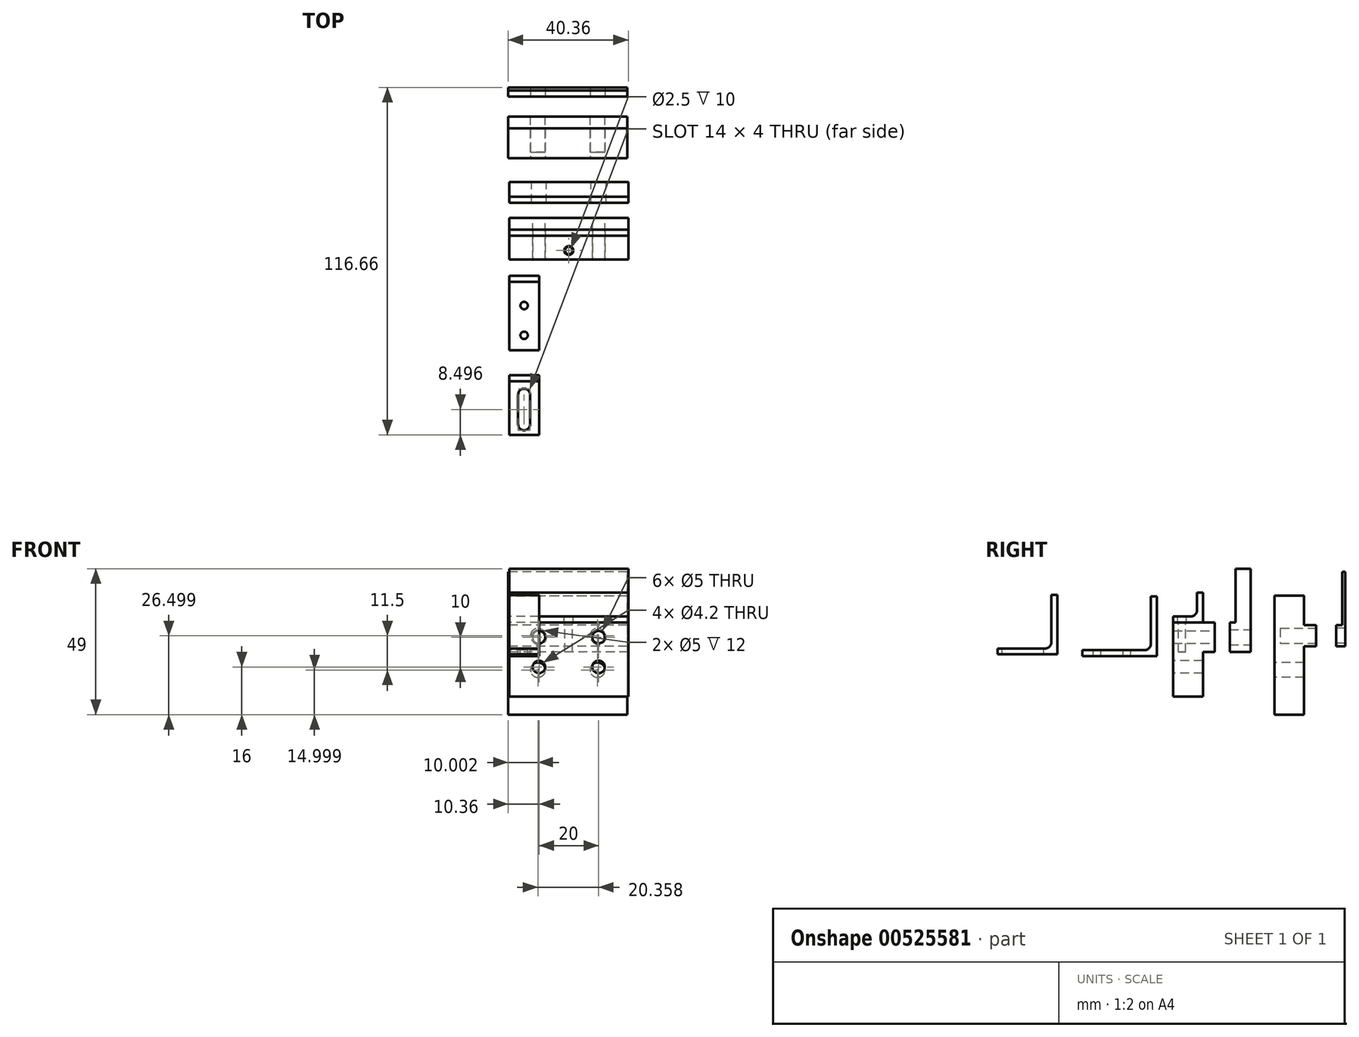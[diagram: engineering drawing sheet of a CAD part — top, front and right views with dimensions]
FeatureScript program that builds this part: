
annotation { "Feature Type Name" : "Feature", "Feature Type Description" : "" }
export const myFeature = defineFeature(function(context is Context, id is Id, definition is map)
    precondition{}
    {
        {
            var Q0;
            Q0=qCreatedBy(makeId("Right.planeOp"),FACE);
            cPlane(context, id + "F0", {"entities" : qUnion([Q0]), "cplaneType" : CPlaneType.OFFSET, "offset" : 40 * mm, "oppositeDirection" : true, "width" : 150 * mm, "height" : 150 * mm});
        }
        {
            var Q0;
            Q0=qCreatedBy(makeId("Front.planeOp"),FACE);
            var sketch = newSketch(context, id + "F1", { "sketchPlane" : qUnion([Q0])});
            skLineSegment(sketch, "E0.bottom", {"start": v(-40.36, 24) * mm, "end": v(-0.36, 24) * mm});
            skLineSegment(sketch, "E0.top", {"start": v(-40.36, -16) * mm, "end": v(-0.36, -16) * mm});
            skLineSegment(sketch, "E0.left", {"start": v(-40.36, 24) * mm, "end": v(-40.36, -16) * mm});
            skLineSegment(sketch, "E0.right", {"start": v(-0.36, 24) * mm, "end": v(-0.36, -16) * mm});
            skCircle(sketch, "E1", {"center": v(-10.36, -1) * mm, "radius": 2.5 * mm});
            skCircle(sketch, "E2", {"center": v(-30.36, -1) * mm, "radius": 2.5 * mm});
            skCircle(sketch, "E3", {"center": v(-30.36, -1) * mm, "radius": 6 * mm, "construction": true});
            skCircle(sketch, "E4", {"center": v(-10.36, -1) * mm, "radius": 6 * mm, "construction": true});
            skSolve(sketch);
        }
        {
            var Q0;
            Q0=qSketchRegion(id+"F1",true);
            extrude(context, id + "F2", {"entities" : qUnion([Q0]), "oppositeDirection" : true, "depth" : 10 * mm});
        }
        {
            var Q0;
            Q0=makeQuery(id+"F2.opExtrude","CAP_FACE",FACE,{"disambiguationData":[OSD([sQuery(id+"F1.wireOp",EDGE,"E0.bottom"),sQuery(id+"F1.wireOp",EDGE,"E0.top"),sQuery(id+"F1.wireOp",EDGE,"E0.left"),sQuery(id+"F1.wireOp",EDGE,"E0.right"),sQuery(id+"F1.wireOp",EDGE,"E1"),sQuery(id+"F1.wireOp",EDGE,"E2")])],"isStart":false});
            var sketch = newSketch(context, id + "F3", { "sketchPlane" : qUnion([Q0])});
            skLineSegment(sketch, "E5.bottom", {"start": v(0.36, 14) * mm, "end": v(40.36, 14) * mm});
            skLineSegment(sketch, "E5.top", {"start": v(0.36, 7) * mm, "end": v(40.36, 7) * mm});
            skLineSegment(sketch, "E5.left", {"start": v(0.36, 14) * mm, "end": v(0.36, 7) * mm});
            skLineSegment(sketch, "E5.right", {"start": v(40.36, 14) * mm, "end": v(40.36, 7) * mm});
            skSolve(sketch);
        }
        {
            var Q0;
            Q0=qSketchRegion(id+"F3",true);
            extrude(context, id + "F4", {"entities" : qUnion([Q0]), "operationType" : NewBodyOperationType.ADD, "depth" : 4 * mm});
        }
        {
            var Q0;
            Q0=makeQuery(id+"F4.opExtrude","CAP_FACE",FACE,{"disambiguationData":[OSD([sQuery(id+"F3.wireOp",EDGE,"E5.bottom"),sQuery(id+"F3.wireOp",EDGE,"E5.top"),sQuery(id+"F3.wireOp",EDGE,"E5.left"),sQuery(id+"F3.wireOp",EDGE,"E5.right")])],"isStart":false});
            var sketch = newSketch(context, id + "F5", { "sketchPlane" : qUnion([Q0])});
            skCircle(sketch, "E6", {"center": v(10.36, 10.5) * mm, "radius": 2.5 * mm});
            skCircle(sketch, "E7", {"center": v(30.36, 10.5) * mm, "radius": 2.5 * mm});
            skSolve(sketch);
        }
        {
            var Q0;
            Q0=qSketchRegion(id+"F5",true);
            extrude(context, id + "F6", {"entities" : qUnion([Q0]), "operationType" : NewBodyOperationType.REMOVE, "oppositeDirection" : true, "depth" : 12 * mm});
        }
        {
            var Q0;
            Q0=makeQuery(id+"F4.boolean.opBoolean","MERGE",FACE,{"derivedFrom":[makeQuery(id+"F2.opExtrude","SWEPT_FACE",FACE,{"disambiguationData":[OSD([sQuery(id+"F1.wireOp",EDGE,"E0.left")])]}),makeQuery(id+"F4.opExtrude","SWEPT_FACE",FACE,{"disambiguationData":[OSD([sQuery(id+"F3.wireOp",EDGE,"E5.right")])]})]});
            var sketch = newSketch(context, id + "F7", { "sketchPlane" : qUnion([Q0])});
            skLineSegment(sketch, "E8", {"start": v(-23.76, 32) * mm, "end": v(-23.76, 7) * mm});
            skLineSegment(sketch, "E9", {"start": v(-20.76, 7) * mm, "end": v(-23.76, 7) * mm});
            skLineSegment(sketch, "E10", {"start": v(-20.76, 7) * mm, "end": v(-20.76, 14) * mm});
            skLineSegment(sketch, "E11", {"start": v(-22.76, 14) * mm, "end": v(-20.76, 14) * mm});
            skLineSegment(sketch, "E12", {"start": v(-22.76, 14) * mm, "end": v(-22.76, 32) * mm});
            skLineSegment(sketch, "E13", {"start": v(-23.76, 32) * mm, "end": v(-22.76, 32) * mm});
            skSolve(sketch);
        }
        {
            var Q0;
            Q0=makeQuery(id+"F7.imprint","IMPRINT",FACE,{"disambiguationData":[TD([[makeQuery(id+"F7.imprint","IMPRINT",EDGE,{"derivedFrom":sQuery(id+"F7.wireOp",EDGE,"E8")}),1.0]])]});
            extrude(context, id + "F8", {"entities" : qUnion([Q0]), "oppositeDirection" : true, "depth" : 40 * mm});
        }
        {
            var Q0;
            Q0=makeQuery(id+"F8.opExtrude","SWEPT_FACE",FACE,{"disambiguationData":[OSD([sQuery(id+"F7.wireOp",EDGE,"E10")])]});
            var sketch = newSketch(context, id + "F9", { "sketchPlane" : qUnion([Q0])});
            skCircle(sketch, "E14", {"center": v(-30.36, 10.5) * mm, "radius": 2.5 * mm});
            skCircle(sketch, "E15", {"center": v(-10.36, 10.5) * mm, "radius": 2.5 * mm});
            skSolve(sketch);
        }
        {
            var Q0;
            Q0=makeQuery(id+"F9.imprint","IMPRINT",FACE,{"disambiguationData":[TD([[makeQuery(id+"F9.imprint","IMPRINT",EDGE,{"derivedFrom":sQuery(id+"F9.wireOp",EDGE,"E14")}),1.0]])]});
            var Q1;
            Q1=makeQuery(id+"F9.imprint","IMPRINT",FACE,{"disambiguationData":[TD([[makeQuery(id+"F9.imprint","IMPRINT",EDGE,{"derivedFrom":sQuery(id+"F9.wireOp",EDGE,"E15")}),1.0]])]});
            extrude(context, id + "F10", {"entities" : qUnion([Q0, Q1]), "operationType" : NewBodyOperationType.REMOVE, "oppositeDirection" : true, "depth" : 3 * mm});
        }
        {
            var Q0;
            Q0=qCreatedBy(id+"F0.planeOp",FACE);
            var sketch = newSketch(context, id + "F11", { "sketchPlane" : qUnion([Q0])});
            skLineSegment(sketch, "E16", {"start": v(-20, 15) * mm, "end": v(-34, 15) * mm});
            skLineSegment(sketch, "E17", {"start": v(-34, 15) * mm, "end": v(-34, -10) * mm});
            skLineSegment(sketch, "E18", {"start": v(-34, -10) * mm, "end": v(-24, -10) * mm});
            skLineSegment(sketch, "E19", {"start": v(-24, -10) * mm, "end": v(-24, 5) * mm});
            skLineSegment(sketch, "E20", {"start": v(-24, 5) * mm, "end": v(-20, 5) * mm});
            skLineSegment(sketch, "E21", {"start": v(-20, 5) * mm, "end": v(-20, 15) * mm});
            skSolve(sketch);
        }
        {
            var Q0;
            Q0=qSketchRegion(id+"F11",true);
            extrude(context, id + "F12", {"entities" : qUnion([Q0]), "depth" : 40 * mm});
        }
        {
            var Q0;
            Q0=qCreatedBy(id+"F0.planeOp",FACE);
            var sketch = newSketch(context, id + "F13", { "sketchPlane" : qUnion([Q0])});
            skLineSegment(sketch, "E22", {"start": v(-8, 33) * mm, "end": v(-8, 5) * mm});
            skLineSegment(sketch, "E23", {"start": v(-8, 5) * mm, "end": v(-15, 5) * mm});
            skLineSegment(sketch, "E24", {"start": v(-15, 5) * mm, "end": v(-15, 15) * mm});
            skLineSegment(sketch, "E25", {"start": v(-15, 15) * mm, "end": v(-13, 15) * mm});
            skLineSegment(sketch, "E26", {"start": v(-13, 15) * mm, "end": v(-13, 33) * mm});
            skLineSegment(sketch, "E27", {"start": v(-13, 33) * mm, "end": v(-8, 33) * mm});
            skSolve(sketch);
        }
        {
            var Q0;
            Q0=makeQuery(id+"F13.imprint","IMPRINT",FACE,{"disambiguationData":[TD([[makeQuery(id+"F13.imprint","IMPRINT",EDGE,{"derivedFrom":sQuery(id+"F13.wireOp",EDGE,"E22")}),-1.0]])]});
            extrude(context, id + "F14", {"entities" : qUnion([Q0]), "depth" : 40 * mm});
        }
        {
            var Q0;
            Q0=makeQuery(id+"F12.opExtrude","SWEPT_FACE",FACE,{"disambiguationData":[OSD([sQuery(id+"F11.wireOp",EDGE,"E17")])]});
            var sketch = newSketch(context, id + "F15", { "sketchPlane" : qUnion([Q0])});
            skCircle(sketch, "E28", {"center": v(-30, 0) * mm, "radius": 2.1 * mm});
            skCircle(sketch, "E29", {"center": v(-10, 0) * mm, "radius": 2.1 * mm});
            skSolve(sketch);
        }
        {
            var Q0;
            Q0=makeQuery(id+"F14.opExtrude","SWEPT_FACE",FACE,{"disambiguationData":[OSD([sQuery(id+"F13.wireOp",EDGE,"E22")])]});
            var sketch = newSketch(context, id + "F16", { "sketchPlane" : qUnion([Q0])});
            skCircle(sketch, "E30", {"center": v(10, 10) * mm, "radius": 2.5 * mm});
            skCircle(sketch, "E31", {"center": v(30, 10) * mm, "radius": 2.5 * mm});
            skSolve(sketch);
        }
        {
            var Q0;
            Q0=qCreatedBy(id+"F0.planeOp",FACE);
            var sketch = newSketch(context, id + "F17", { "sketchPlane" : qUnion([Q0])});
            skLineSegment(sketch, "E32", {"start": v(-24, 25) * mm, "end": v(-24, 15) * mm});
            skLineSegment(sketch, "E33", {"start": v(-24, 15) * mm, "end": v(-34, 15) * mm});
            skLineSegment(sketch, "E34", {"start": v(-34, 15) * mm, "end": v(-34, 17) * mm});
            skLineSegment(sketch, "E35", {"start": v(-34, 17) * mm, "end": v(-28, 17) * mm});
            skLineSegment(sketch, "E36", {"start": v(-26, 19) * mm, "end": v(-26, 25) * mm});
            skLineSegment(sketch, "E37", {"start": v(-26, 25) * mm, "end": v(-24, 25) * mm});
            skPoint(sketch, "E38.visualSharp", {"position": v(-26, 17) * mm});
            skArc(sketch, "E38.filletArc", {"start": v(-28, 17) * mm, "mid": v(-26.59, 17.59) * mm, "end": v(-26, 19) * mm});
            skSolve(sketch);
        }
        {
            var Q0;
            Q0=makeQuery(id+"F17.imprint","IMPRINT",FACE,{"disambiguationData":[TD([[makeQuery(id+"F17.imprint","IMPRINT",EDGE,{"derivedFrom":sQuery(id+"F17.wireOp",EDGE,"E32")}),-1.0]])]});
            extrude(context, id + "F18", {"entities" : qUnion([Q0]), "depth" : 40 * mm});
        }
        {
            var Q0;
            Q0=makeQuery(id+"F18.opExtrude","SWEPT_FACE",FACE,{"disambiguationData":[OSD([sQuery(id+"F17.wireOp",EDGE,"E35")])]});
            var sketch = newSketch(context, id + "F19", { "sketchPlane" : qUnion([Q0])});
            skCircle(sketch, "E39", {"center": v(-20, -31) * mm, "radius": 1.25 * mm});
            skSolve(sketch);
        }
        {
            var Q0;
            Q0=makeQuery(id+"F15.imprint","IMPRINT",FACE,{"disambiguationData":[TD([[makeQuery(id+"F15.imprint","IMPRINT",EDGE,{"derivedFrom":sQuery(id+"F15.wireOp",EDGE,"E28")}),1.0]])]});
            var Q1;
            Q1=makeQuery(id+"F15.imprint","IMPRINT",FACE,{"disambiguationData":[TD([[makeQuery(id+"F15.imprint","IMPRINT",EDGE,{"derivedFrom":sQuery(id+"F15.wireOp",EDGE,"E29")}),1.0]])]});
            extrude(context, id + "F20", {"entities" : qUnion([Q0, Q1]), "operationType" : NewBodyOperationType.REMOVE, "oppositeDirection" : true, "depth" : 10 * mm});
        }
        {
            var Q0;
            Q0=makeQuery(id+"F16.imprint","IMPRINT",FACE,{"disambiguationData":[TD([[makeQuery(id+"F16.imprint","IMPRINT",EDGE,{"derivedFrom":sQuery(id+"F16.wireOp",EDGE,"E30")}),1.0]])]});
            var Q1;
            Q1=makeQuery(id+"F16.imprint","IMPRINT",FACE,{"disambiguationData":[TD([[makeQuery(id+"F16.imprint","IMPRINT",EDGE,{"derivedFrom":sQuery(id+"F16.wireOp",EDGE,"E31")}),1.0]])]});
            extrude(context, id + "F21", {"entities" : qUnion([Q0, Q1]), "operationType" : NewBodyOperationType.REMOVE, "oppositeDirection" : true, "depth" : 7 * mm});
        }
        {
            var Q0;
            Q0=makeQuery(id+"F19.imprint","IMPRINT",FACE,{"disambiguationData":[TD([[makeQuery(id+"F19.imprint","IMPRINT",EDGE,{"derivedFrom":sQuery(id+"F19.wireOp",EDGE,"nTF4TsUg-xscX-gh34-UHNV-MDi5rEr1EhpZ")}),1.0]])]});
            var Q1;
            Q1=makeQuery(id+"F19.imprint","IMPRINT",FACE,{"disambiguationData":[TD([[makeQuery(id+"F19.imprint","IMPRINT",EDGE,{"derivedFrom":sQuery(id+"F19.wireOp",EDGE,"E39")}),1.0]])]});
            extrude(context, id + "F22", {"entities" : qUnion([Q0, Q1]), "operationType" : NewBodyOperationType.REMOVE, "oppositeDirection" : true, "depth" : 12 * mm});
        }
        {
            var Q0;
            Q0=qCreatedBy(id+"F0.planeOp",FACE);
            var sketch = newSketch(context, id + "F23", { "sketchPlane" : qUnion([Q0])});
            skLineSegment(sketch, "E40", {"start": v(-39.5, 23.68) * mm, "end": v(-39.5, 3.68) * mm});
            skLineSegment(sketch, "E41", {"start": v(-39.5, 3.68) * mm, "end": v(-64.5, 3.68) * mm});
            skLineSegment(sketch, "E42", {"start": v(-64.5, 3.68) * mm, "end": v(-64.5, 5.68) * mm});
            skLineSegment(sketch, "E43", {"start": v(-64.5, 5.68) * mm, "end": v(-43.5, 5.68) * mm});
            skLineSegment(sketch, "E44", {"start": v(-41.5, 7.68) * mm, "end": v(-41.5, 23.68) * mm});
            skLineSegment(sketch, "E45", {"start": v(-41.5, 23.68) * mm, "end": v(-39.5, 23.68) * mm});
            skPoint(sketch, "E46.visualSharp", {"position": v(-41.5, 5.68) * mm});
            skArc(sketch, "E46.filletArc", {"start": v(-43.5, 5.68) * mm, "mid": v(-42.08, 6.26) * mm, "end": v(-41.5, 7.68) * mm});
            skSolve(sketch);
        }
        {
            var Q0;
            Q0=makeQuery(id+"F23.imprint","IMPRINT",FACE,{"disambiguationData":[TD([[makeQuery(id+"F23.imprint","IMPRINT",EDGE,{"derivedFrom":sQuery(id+"F23.wireOp",EDGE,"E40")}),-1.0]])]});
            extrude(context, id + "F24", {"entities" : qUnion([Q0]), "depth" : 10 * mm});
        }
        {
            var Q0;
            Q0=makeQuery(id+"F24.opExtrude","SWEPT_FACE",FACE,{"disambiguationData":[OSD([sQuery(id+"F23.wireOp",EDGE,"E43")])]});
            var sketch = newSketch(context, id + "F25", { "sketchPlane" : qUnion([Q0])});
            skCircle(sketch, "E47", {"center": v(-35, -49.5) * mm, "radius": 1.25 * mm});
            skCircle(sketch, "E48", {"center": v(-35, -59.5) * mm, "radius": 1.25 * mm});
            skSolve(sketch);
        }
        {
            var Q0;
            Q0=makeQuery(id+"F25.imprint","IMPRINT",FACE,{"disambiguationData":[TD([[makeQuery(id+"F25.imprint","IMPRINT",EDGE,{"derivedFrom":sQuery(id+"F25.wireOp",EDGE,"E47")}),1.0]])]});
            var Q1;
            Q1=makeQuery(id+"F25.imprint","IMPRINT",FACE,{"disambiguationData":[TD([[makeQuery(id+"F25.imprint","IMPRINT",EDGE,{"derivedFrom":sQuery(id+"F25.wireOp",EDGE,"E48")}),1.0]])]});
            extrude(context, id + "F26", {"entities" : qUnion([Q0, Q1]), "operationType" : NewBodyOperationType.REMOVE, "oppositeDirection" : true, "depth" : 2 * mm});
        }
        {
            var Q0;
            Q0=qCreatedBy(id+"F0.planeOp",FACE);
            var sketch = newSketch(context, id + "F27", { "sketchPlane" : qUnion([Q0])});
            skLineSegment(sketch, "E49", {"start": v(-72.9, 24.22) * mm, "end": v(-72.9, 4.22) * mm});
            skLineSegment(sketch, "E50", {"start": v(-72.9, 4.22) * mm, "end": v(-92.9, 4.22) * mm});
            skLineSegment(sketch, "E51", {"start": v(-92.9, 4.22) * mm, "end": v(-92.9, 6.22) * mm});
            skLineSegment(sketch, "E52", {"start": v(-92.9, 6.22) * mm, "end": v(-76.9, 6.22) * mm});
            skLineSegment(sketch, "E53", {"start": v(-74.9, 8.22) * mm, "end": v(-74.9, 24.22) * mm});
            skLineSegment(sketch, "E54", {"start": v(-74.9, 24.22) * mm, "end": v(-72.9, 24.22) * mm});
            skPoint(sketch, "E55.visualSharp", {"position": v(-74.9, 6.22) * mm});
            skArc(sketch, "E55.filletArc", {"start": v(-76.9, 6.22) * mm, "mid": v(-75.5, 6.8) * mm, "end": v(-74.9, 8.22) * mm});
            skSolve(sketch);
        }
        {
            var Q0;
            Q0=makeQuery(id+"F27.imprint","IMPRINT",FACE,{"disambiguationData":[TD([[makeQuery(id+"F27.imprint","IMPRINT",EDGE,{"derivedFrom":sQuery(id+"F27.wireOp",EDGE,"E49")}),-1.0]])]});
            var Q1;
            Q1=sQuery(id+"F27.wireOp",EDGE,"E49");
            var Q2;
            Q2=sQuery(id+"F27.wireOp",EDGE,"E50");
            var Q3;
            Q3=sQuery(id+"F27.wireOp",EDGE,"E51");
            var Q4;
            Q4=sQuery(id+"F27.wireOp",EDGE,"E52");
            var Q5;
            Q5=sQuery(id+"F27.wireOp",EDGE,"E53");
            var Q6;
            Q6=sQuery(id+"F27.wireOp",EDGE,"E54");
            extrude(context, id + "F28", {"entities" : qUnion([Q0]), "surfaceEntities" : qUnion([Q1, Q2, Q3, Q4, Q5, Q6]), "depth" : 10 * mm});
        }
        {
            var Q0;
            Q0=makeQuery(id+"F28.opExtrude","SWEPT_FACE",FACE,{"disambiguationData":[OSD([sQuery(id+"F27.wireOp",EDGE,"E52")])]});
            var sketch = newSketch(context, id + "F29", { "sketchPlane" : qUnion([Q0])});
            skLineSegment(sketch, "E56.left", {"start": v(-37, -89.4) * mm, "end": v(-37, -79.4) * mm});
            skLineSegment(sketch, "E56.right", {"start": v(-33, -89.4) * mm, "end": v(-33, -79.4) * mm});
            skPoint(sketch, "E56.middle", {"position": v(-35, -84.4) * mm});
            skArc(sketch, "E57", {"start": v(-37, -89.4) * mm, "mid": v(-35, -91.4) * mm, "end": v(-33, -89.4) * mm});
            skArc(sketch, "E58", {"start": v(-33, -79.4) * mm, "mid": v(-35, -77.4) * mm, "end": v(-37, -79.4) * mm});
            skSolve(sketch);
        }
        {
            var Q0;
            Q0=makeQuery(id+"F29.imprint","IMPRINT",FACE,{"disambiguationData":[TD([[makeQuery(id+"F29.imprint","IMPRINT",EDGE,{"derivedFrom":sQuery(id+"F29.wireOp",EDGE,"E56.left")}),-1.0]])]});
            extrude(context, id + "F30", {"entities" : qUnion([Q0]), "operationType" : NewBodyOperationType.REMOVE, "oppositeDirection" : true, "depth" : 3 * mm});
        }
        {
            var Q0;
            Q0=makeQuery(id+"F12.opExtrude","SWEPT_FACE",FACE,{"disambiguationData":[OSD([sQuery(id+"F11.wireOp",EDGE,"E21")])]});
            var sketch = newSketch(context, id + "F31", { "sketchPlane" : qUnion([Q0])});
            skCircle(sketch, "E59", {"center": v(30, 10) * mm, "radius": 2.1 * mm});
            skCircle(sketch, "E60", {"center": v(10, 10) * mm, "radius": 2.1 * mm});
            skSolve(sketch);
        }
        {
            var Q0;
            Q0=qSketchRegion(id+"F31",true);
            extrude(context, id + "F32", {"entities" : qUnion([Q0]), "operationType" : NewBodyOperationType.REMOVE, "oppositeDirection" : true, "depth" : 14 * mm});
        }
        {
            var Q0;
            Q0=sQuery(id+"F19.wireOp",VERTEX,"E39.center");
            var Q1;
            Q1=makeQuery(id+"F18.opExtrude","SWEPT_BODY",BODY,{"disambiguationData":[OSD([sQuery(id+"F17.wireOp",EDGE,"E32"),sQuery(id+"F17.wireOp",EDGE,"E33"),sQuery(id+"F17.wireOp",EDGE,"E34"),sQuery(id+"F17.wireOp",EDGE,"E35"),sQuery(id+"F17.wireOp",EDGE,"E36"),sQuery(id+"F17.wireOp",EDGE,"E37"),sQuery(id+"F17.wireOp",EDGE,"E38.filletArc")])]});
            hole(context, id + "F33", {"style" : HoleStyle.SIMPLE, "endStyle" : HoleEndStyle.THROUGH, "holeDiameter" : 3 * mm, "locations" : qUnion([Q0]), "scope" : qUnion([Q1]), "isTappedThrough" : true});
        }
    });
